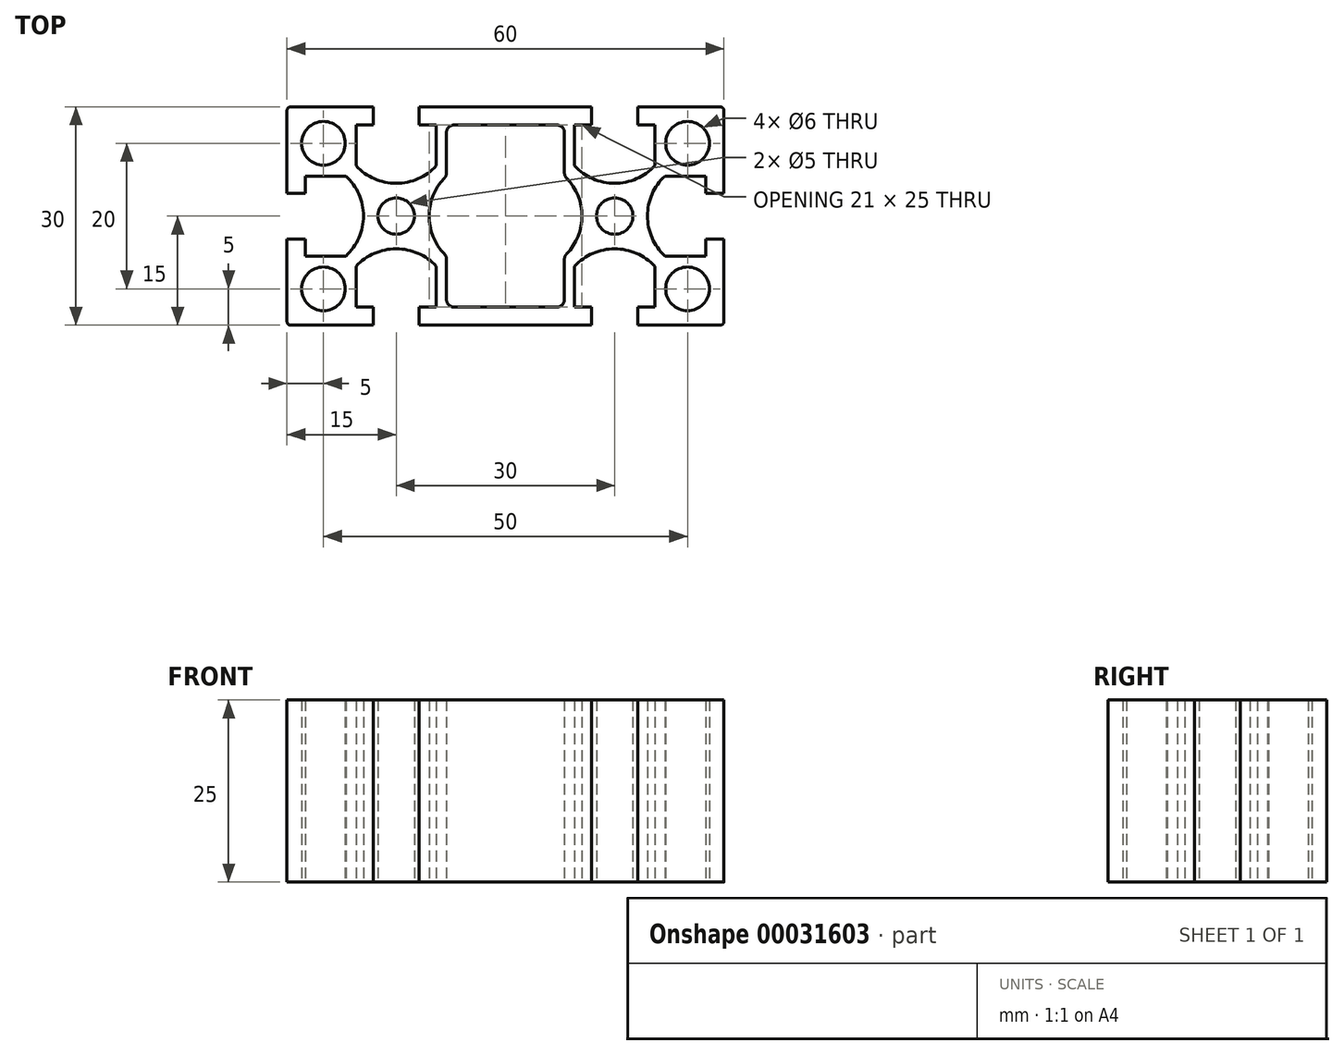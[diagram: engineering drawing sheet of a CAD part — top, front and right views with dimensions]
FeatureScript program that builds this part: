
annotation { "Feature Type Name" : "Feature", "Feature Type Description" : "" }
export const myFeature = defineFeature(function(context is Context, id is Id, definition is map)
    precondition{}
    {
        {
            var Q0;
            Q0=qCreatedBy(makeId("Top.planeOp"),FACE);
            var sketch = newSketch(context, id + "F0", { "sketchPlane" : qUnion([Q0])});
            skCircle(sketch, "E0", {"center": v(0, 0) * mm, "radius": 2.5 * mm});
            skLineSegment(sketch, "E1", {"start": v(0, 0) * mm, "end": v(-15, 0) * mm, "construction": true});
            skLineSegment(sketch, "E2", {"start": v(-15, 0) * mm, "end": v(-15, 15) * mm, "construction": true});
            skLineSegment(sketch, "E3", {"start": v(-15, 15) * mm, "end": v(0, 15) * mm, "construction": true});
            skLineSegment(sketch, "E4", {"start": v(0, 15) * mm, "end": v(0, 0) * mm, "construction": true});
            skLineSegment(sketch, "E5", {"start": v(-15, 15) * mm, "end": v(0, 0) * mm, "construction": true});
            skLineSegment(sketch, "E6", {"start": v(-15, 10) * mm, "end": v(-10, 10) * mm, "construction": true});
            skPoint(sketch, "E7", {"position": v(-15, 3.15) * mm});
            skPoint(sketch, "E8", {"position": v(-15, 5.5) * mm});
            skCircle(sketch, "E9", {"center": v(-10, 10) * mm, "radius": 3 * mm});
            skLineSegment(sketch, "E10", {"start": v(-15, 14.5) * mm, "end": v(-15, 3.15) * mm});
            skLineSegment(sketch, "E11", {"start": v(-15, 3.15) * mm, "end": v(-12.5, 3.15) * mm});
            skLineSegment(sketch, "E12", {"start": v(-12.5, 3.15) * mm, "end": v(-12.5, 5.5) * mm});
            skPoint(sketch, "E13", {"position": v(-4.5, 0) * mm});
            skLineSegment(sketch, "E14", {"start": v(-12.5, 5.5) * mm, "end": v(-5.5, 5.5) * mm, "construction": true});
            skArc(sketch, "E15", {"start": v(-4.5, 0) * mm, "mid": v(-5.13, 3) * mm, "end": v(-6.9, 5.5) * mm});
            skLineSegment(sketch, "E16", {"start": v(-12.5, 5.5) * mm, "end": v(-6.9, 5.5) * mm});
            skLineSegment(sketch, "E17.0.MirrorCS", {"start": v(-14.5, 15) * mm, "end": v(-3.15, 15) * mm});
            skPoint(sketch, "E18.visualSharp", {"position": v(-15, 15) * mm});
            skArc(sketch, "E18.filletArc", {"start": v(-14.5, 15) * mm, "mid": v(-14.85, 14.85) * mm, "end": v(-15, 14.5) * mm});
            skLineSegment(sketch, "E19.0.MirrorCS", {"start": v(-3.15, 15) * mm, "end": v(-3.15, 12.5) * mm});
            skLineSegment(sketch, "E20.0.MirrorCS", {"start": v(-3.15, 12.5) * mm, "end": v(-5.5, 12.5) * mm});
            skLineSegment(sketch, "E21.0.MirrorCS", {"start": v(-5.5, 12.5) * mm, "end": v(-5.5, 6.9) * mm});
            skArc(sketch, "E22.0.MirrorCS", {"start": v(0, 4.5) * mm, "mid": v(-3, 5.13) * mm, "end": v(-5.5, 6.9) * mm});
            skArc(sketch, "E23.0.MirrorCS", {"start": v(-4.5, 0) * mm, "mid": v(-5.13, -3) * mm, "end": v(-6.9, -5.5) * mm});
            skLineSegment(sketch, "E24.0.MirrorCS", {"start": v(-12.5, -5.5) * mm, "end": v(-6.9, -5.5) * mm});
            skLineSegment(sketch, "E25.0.MirrorCS", {"start": v(-12.5, -3.15) * mm, "end": v(-12.5, -5.5) * mm});
            skLineSegment(sketch, "E26.0.MirrorCS", {"start": v(-15, -3.15) * mm, "end": v(-12.5, -3.15) * mm});
            skLineSegment(sketch, "E27.0.MirrorCS", {"start": v(-15, -14.5) * mm, "end": v(-15, -3.15) * mm});
            skArc(sketch, "E28.0.MirrorCS", {"start": v(-14.5, -15) * mm, "mid": v(-14.85, -14.85) * mm, "end": v(-15, -14.5) * mm});
            skLineSegment(sketch, "E29.0.MirrorCS", {"start": v(-14.5, -15) * mm, "end": v(-3.15, -15) * mm});
            skLineSegment(sketch, "E30.0.MirrorCS", {"start": v(-3.15, -15) * mm, "end": v(-3.15, -12.5) * mm});
            skLineSegment(sketch, "E31.0.MirrorCS", {"start": v(-3.15, -12.5) * mm, "end": v(-5.5, -12.5) * mm});
            skLineSegment(sketch, "E32.0.MirrorCS", {"start": v(-5.5, -12.5) * mm, "end": v(-5.5, -6.9) * mm});
            skArc(sketch, "E33.0.MirrorCS", {"start": v(0, -4.5) * mm, "mid": v(-3, -5.13) * mm, "end": v(-5.5, -6.9) * mm});
            skCircle(sketch, "E34.0.MirrorC", {"center": v(-10, -10) * mm, "radius": 3 * mm});
            skArc(sketch, "E35.0.MirrorCS", {"start": v(0, 4.5) * mm, "mid": v(3, 5.13) * mm, "end": v(5.5, 6.9) * mm});
            skLineSegment(sketch, "E36.0.MirrorCS", {"start": v(5.5, 12.5) * mm, "end": v(5.5, 6.9) * mm});
            skLineSegment(sketch, "E37.0.MirrorCS", {"start": v(3.15, 12.5) * mm, "end": v(5.5, 12.5) * mm});
            skLineSegment(sketch, "E38.0.MirrorCS", {"start": v(3.15, 15) * mm, "end": v(3.15, 12.5) * mm});
            skArc(sketch, "E39.0.MirrorCS", {"start": v(0, -4.5) * mm, "mid": v(3, -5.13) * mm, "end": v(5.5, -6.9) * mm});
            skLineSegment(sketch, "E40.0.MirrorCS", {"start": v(5.5, -12.5) * mm, "end": v(5.5, -6.9) * mm});
            skLineSegment(sketch, "E41.0.MirrorCS", {"start": v(3.15, -12.5) * mm, "end": v(5.5, -12.5) * mm});
            skLineSegment(sketch, "E42.0.MirrorCS", {"start": v(3.15, -15) * mm, "end": v(3.15, -12.5) * mm});
            skLineSegment(sketch, "E43", {"start": v(0, 0) * mm, "end": v(30, 0) * mm, "construction": true});
            skPoint(sketch, "E44", {"position": v(15, 0) * mm});
            skLineSegment(sketch, "E45", {"start": v(15, 15) * mm, "end": v(15, -15) * mm, "construction": true});
            skCircle(sketch, "E46.0.MirrorC", {"center": v(30, 0) * mm, "radius": 2.5 * mm});
            skLineSegment(sketch, "E47.0.MirrorCS", {"start": v(26.85, 15) * mm, "end": v(26.85, 12.5) * mm});
            skLineSegment(sketch, "E48.0.MirrorCS", {"start": v(26.85, 12.5) * mm, "end": v(24.5, 12.5) * mm});
            skLineSegment(sketch, "E49.0.MirrorCS", {"start": v(24.5, 12.5) * mm, "end": v(24.5, 6.9) * mm});
            skArc(sketch, "E50.0.MirrorCS", {"start": v(30, 4.5) * mm, "mid": v(27, 5.13) * mm, "end": v(24.5, 6.9) * mm});
            skArc(sketch, "E51.0.MirrorCS", {"start": v(30, 4.5) * mm, "mid": v(33, 5.13) * mm, "end": v(35.5, 6.9) * mm});
            skLineSegment(sketch, "E52.0.MirrorCS", {"start": v(35.5, 12.5) * mm, "end": v(35.5, 6.9) * mm});
            skLineSegment(sketch, "E53.0.MirrorCS", {"start": v(33.15, 12.5) * mm, "end": v(35.5, 12.5) * mm});
            skLineSegment(sketch, "E54.0.MirrorCS", {"start": v(33.15, 15) * mm, "end": v(33.15, 12.5) * mm});
            skLineSegment(sketch, "E55.0.MirrorCS", {"start": v(44.5, 15) * mm, "end": v(33.15, 15) * mm});
            skArc(sketch, "E56.0.MirrorCS", {"start": v(44.5, 15) * mm, "mid": v(44.85, 14.85) * mm, "end": v(45, 14.5) * mm});
            skLineSegment(sketch, "E57.0.MirrorCS", {"start": v(45, 14.5) * mm, "end": v(45, 3.15) * mm});
            skLineSegment(sketch, "E58.0.MirrorCS", {"start": v(45, 3.15) * mm, "end": v(42.5, 3.15) * mm});
            skLineSegment(sketch, "E59.0.MirrorCS", {"start": v(42.5, 3.15) * mm, "end": v(42.5, 5.5) * mm});
            skLineSegment(sketch, "E60.0.MirrorCS", {"start": v(42.5, 5.5) * mm, "end": v(36.9, 5.5) * mm});
            skArc(sketch, "E61.0.MirrorCS", {"start": v(34.5, 0) * mm, "mid": v(35.13, 3) * mm, "end": v(36.9, 5.5) * mm});
            skArc(sketch, "E62.0.MirrorCS", {"start": v(34.5, 0) * mm, "mid": v(35.13, -3) * mm, "end": v(36.9, -5.5) * mm});
            skLineSegment(sketch, "E63.0.MirrorCS", {"start": v(42.5, -5.5) * mm, "end": v(36.9, -5.5) * mm});
            skLineSegment(sketch, "E64.0.MirrorCS", {"start": v(42.5, -3.15) * mm, "end": v(42.5, -5.5) * mm});
            skLineSegment(sketch, "E65.0.MirrorCS", {"start": v(45, -3.15) * mm, "end": v(42.5, -3.15) * mm});
            skLineSegment(sketch, "E66.0.MirrorCS", {"start": v(45, -14.5) * mm, "end": v(45, -3.15) * mm});
            skArc(sketch, "E67.0.MirrorCS", {"start": v(44.5, -15) * mm, "mid": v(44.85, -14.85) * mm, "end": v(45, -14.5) * mm});
            skLineSegment(sketch, "E68.0.MirrorCS", {"start": v(44.5, -15) * mm, "end": v(33.15, -15) * mm});
            skLineSegment(sketch, "E69.0.MirrorCS", {"start": v(33.15, -15) * mm, "end": v(33.15, -12.5) * mm});
            skLineSegment(sketch, "E70.0.MirrorCS", {"start": v(33.15, -12.5) * mm, "end": v(35.5, -12.5) * mm});
            skLineSegment(sketch, "E71.0.MirrorCS", {"start": v(35.5, -12.5) * mm, "end": v(35.5, -6.9) * mm});
            skArc(sketch, "E72.0.MirrorCS", {"start": v(30, -4.5) * mm, "mid": v(33, -5.13) * mm, "end": v(35.5, -6.9) * mm});
            skArc(sketch, "E73.0.MirrorCS", {"start": v(30, -4.5) * mm, "mid": v(27, -5.13) * mm, "end": v(24.5, -6.9) * mm});
            skLineSegment(sketch, "E74.0.MirrorCS", {"start": v(24.5, -12.5) * mm, "end": v(24.5, -6.9) * mm});
            skLineSegment(sketch, "E75.0.MirrorCS", {"start": v(26.85, -12.5) * mm, "end": v(24.5, -12.5) * mm});
            skLineSegment(sketch, "E76.0.MirrorCS", {"start": v(26.85, -15) * mm, "end": v(26.85, -12.5) * mm});
            skCircle(sketch, "E77.0.MirrorC", {"center": v(40, -10) * mm, "radius": 3 * mm});
            skCircle(sketch, "E78.0.MirrorC", {"center": v(40, 10) * mm, "radius": 3 * mm});
            skLineSegment(sketch, "E79", {"start": v(3.15, 15) * mm, "end": v(26.85, 15) * mm});
            skLineSegment(sketch, "E80", {"start": v(3.15, -15) * mm, "end": v(26.85, -15) * mm});
            skLineSegment(sketch, "E81.0.MirrorCS", {"start": v(0, 15) * mm, "end": v(0, 30) * mm, "construction": true});
            skArc(sketch, "E82.0.MirrorCS", {"start": v(-4.5, 30) * mm, "mid": v(-5.13, 27) * mm, "end": v(-6.9, 24.5) * mm});
            skArc(sketch, "E83.0.MirrorCS", {"start": v(-4.5, 30) * mm, "mid": v(-5.13, 33) * mm, "end": v(-6.9, 35.5) * mm});
            skArc(sketch, "E84.0.MirrorCS", {"start": v(4.5, 0) * mm, "mid": v(5.05, 2.82) * mm, "end": v(6.62, 5.22) * mm});
            skLineSegment(sketch, "E85", {"start": v(6.9, 5.92) * mm, "end": v(6.9, 11.5) * mm});
            skLineSegment(sketch, "E86", {"start": v(7.9, 12.5) * mm, "end": v(15, 12.5) * mm});
            skPoint(sketch, "E87.visualSharp", {"position": v(6.9, 5.5) * mm});
            skArc(sketch, "E87.filletArc", {"start": v(6.62, 5.22) * mm, "mid": v(6.83, 5.54) * mm, "end": v(6.9, 5.92) * mm});
            skPoint(sketch, "E88.visualSharp", {"position": v(6.9, 12.5) * mm});
            skArc(sketch, "E88.filletArc", {"start": v(7.9, 12.5) * mm, "mid": v(7.2, 12.2) * mm, "end": v(6.9, 11.5) * mm});
            skPoint(sketch, "E89", {"position": v(15, 12.5) * mm});
            skLineSegment(sketch, "E90.0.MirrorCS", {"start": v(22.1, 12.5) * mm, "end": v(15, 12.5) * mm});
            skArc(sketch, "E91.0.MirrorCS", {"start": v(22.1, 12.5) * mm, "mid": v(22.8, 12.2) * mm, "end": v(23.1, 11.5) * mm});
            skLineSegment(sketch, "E92.0.MirrorCS", {"start": v(23.1, 5.92) * mm, "end": v(23.1, 11.5) * mm});
            skArc(sketch, "E93.0.MirrorCS", {"start": v(23.38, 5.22) * mm, "mid": v(23.17, 5.54) * mm, "end": v(23.1, 5.92) * mm});
            skArc(sketch, "E94.0.MirrorCS", {"start": v(25.5, 0) * mm, "mid": v(24.95, 2.82) * mm, "end": v(23.38, 5.22) * mm});
            skArc(sketch, "E95.0.MirrorCS", {"start": v(4.5, 0) * mm, "mid": v(5.05, -2.82) * mm, "end": v(6.62, -5.22) * mm});
            skPoint(sketch, "E96.0.MirrorP", {"position": v(6.9, -5.5) * mm});
            skArc(sketch, "E97.0.MirrorCS", {"start": v(6.62, -5.22) * mm, "mid": v(6.83, -5.54) * mm, "end": v(6.9, -5.92) * mm});
            skLineSegment(sketch, "E98.0.MirrorCS", {"start": v(6.9, -5.92) * mm, "end": v(6.9, -11.5) * mm});
            skLineSegment(sketch, "E99.0.MirrorCS", {"start": v(7.9, -12.5) * mm, "end": v(15, -12.5) * mm});
            skArc(sketch, "E100.0.MirrorCS", {"start": v(7.9, -12.5) * mm, "mid": v(7.2, -12.2) * mm, "end": v(6.9, -11.5) * mm});
            skLineSegment(sketch, "E101.0.MirrorCS", {"start": v(22.1, -12.5) * mm, "end": v(15, -12.5) * mm});
            skArc(sketch, "E102.0.MirrorCS", {"start": v(22.1, -12.5) * mm, "mid": v(22.8, -12.2) * mm, "end": v(23.1, -11.5) * mm});
            skLineSegment(sketch, "E103.0.MirrorCS", {"start": v(23.1, -5.92) * mm, "end": v(23.1, -11.5) * mm});
            skArc(sketch, "E104.0.MirrorCS", {"start": v(23.38, -5.22) * mm, "mid": v(23.17, -5.54) * mm, "end": v(23.1, -5.92) * mm});
            skArc(sketch, "E105.0.MirrorCS", {"start": v(25.5, 0) * mm, "mid": v(24.95, -2.82) * mm, "end": v(23.38, -5.22) * mm});
            skSolve(sketch);
        }
        {
            var Q0;
            Q0=qSketchRegion(id+"F0",true);
            extrude(context, id + "F1", {"entities" : qUnion([Q0]), "depth" : 25 * mm});
        }
    });
